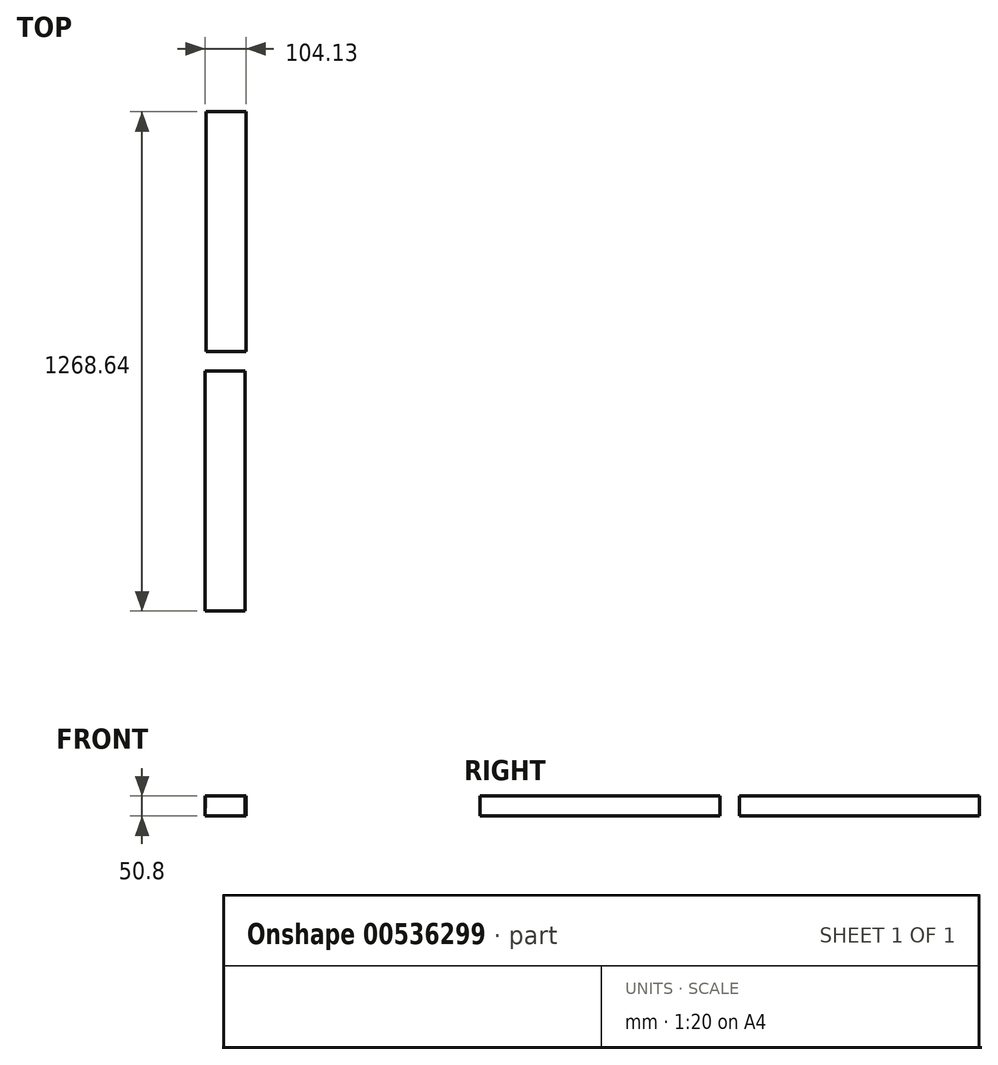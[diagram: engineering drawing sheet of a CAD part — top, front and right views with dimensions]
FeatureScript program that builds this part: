
annotation { "Feature Type Name" : "Feature", "Feature Type Description" : "" }
export const myFeature = defineFeature(function(context is Context, id is Id, definition is map)
    precondition{}
    {
        {
            var Q0;
            Q0=qCreatedBy(makeId("Top.planeOp"),FACE);
            var sketch = newSketch(context, id + "F0", { "sketchPlane" : qUnion([Q0])});
            skLineSegment(sketch, "E0.bottom", {"start": v(-51.44, 659.04) * mm, "end": v(50.16, 659.04) * mm});
            skLineSegment(sketch, "E0.top", {"start": v(-51.44, 49.44) * mm, "end": v(50.16, 49.44) * mm});
            skLineSegment(sketch, "E0.left", {"start": v(-51.44, 659.04) * mm, "end": v(-51.44, 49.44) * mm});
            skLineSegment(sketch, "E0.right", {"start": v(50.16, 659.04) * mm, "end": v(50.16, 49.44) * mm});
            skLineSegment(sketch, "E1.bottom", {"start": v(-53.97, 0) * mm, "end": v(47.63, 0) * mm});
            skLineSegment(sketch, "E1.top", {"start": v(-53.97, -609.6) * mm, "end": v(47.63, -609.6) * mm});
            skLineSegment(sketch, "E1.left", {"start": v(-53.97, 0) * mm, "end": v(-53.97, -609.6) * mm});
            skLineSegment(sketch, "E1.right", {"start": v(47.63, 0) * mm, "end": v(47.63, -609.6) * mm});
            skSolve(sketch);
        }
        {
            var Q0;
            Q0=makeQuery(id+"F0.imprint","IMPRINT",FACE,{"disambiguationData":[TD([[makeQuery(id+"F0.imprint","IMPRINT",EDGE,{"derivedFrom":sQuery(id+"F0.wireOp",EDGE,"E0.bottom")}),-1.0]])]});
            var Q1;
            Q1=makeQuery(id+"F0.imprint","IMPRINT",FACE,{"disambiguationData":[TD([[makeQuery(id+"F0.imprint","IMPRINT",EDGE,{"derivedFrom":sQuery(id+"F0.wireOp",EDGE,"E1.bottom")}),-1.0]])]});
            extrude(context, id + "F1", {"entities" : qUnion([Q0, Q1]), "depth" : 50.8 * mm, "offsetDistance" : 25.4 * mm});
        }
        {
            var Q0;
            Q0=makeQuery(id+"F0.imprint","IMPRINT",FACE,{"disambiguationData":[TD([[makeQuery(id+"F0.imprint","IMPRINT",EDGE,{"derivedFrom":sQuery(id+"F0.wireOp",EDGE,"E1.bottom")}),-1.0]])]});
            extrude(context, id + "F2", {"entities" : qUnion([Q0]), "operationType" : NewBodyOperationType.ADD, "depth" : 50.8 * mm, "offsetDistance" : 25.4 * mm});
        }
    });
